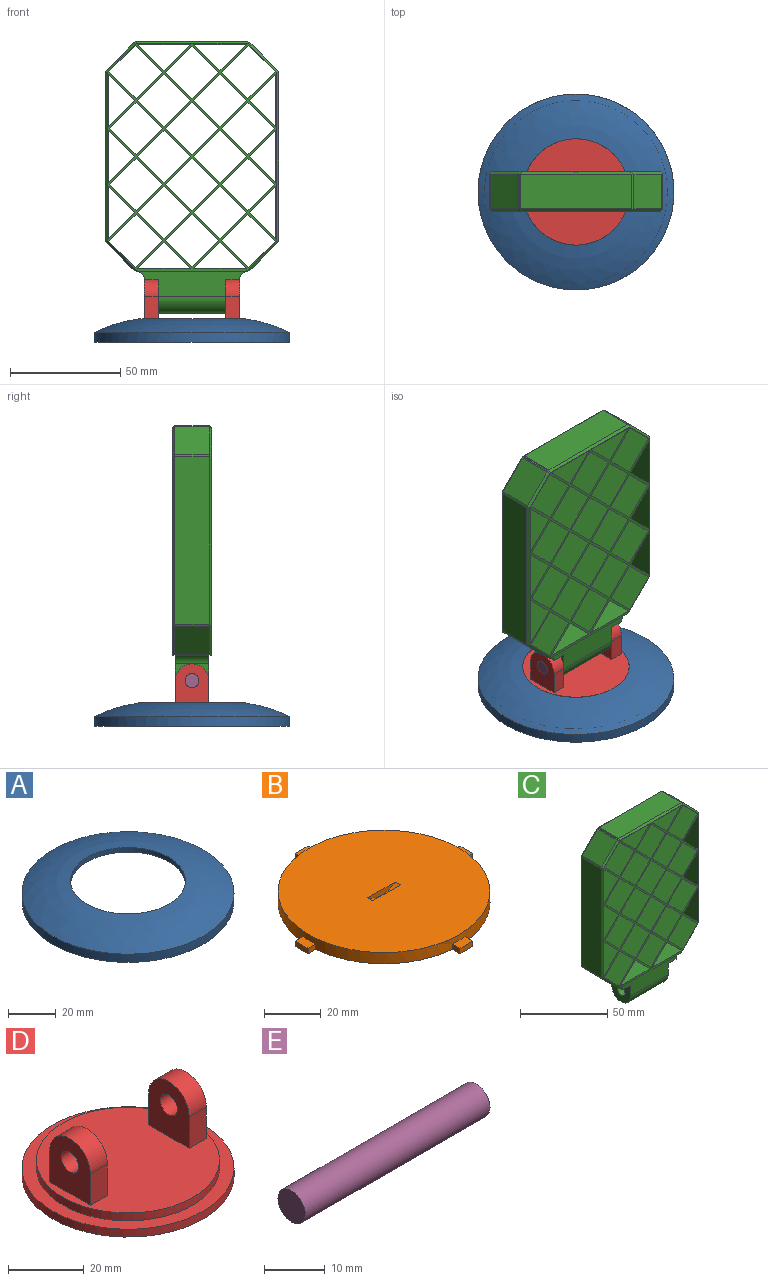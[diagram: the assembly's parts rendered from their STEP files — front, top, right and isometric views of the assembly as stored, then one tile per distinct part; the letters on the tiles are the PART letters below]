
ASSEMBLY  parts=5 mates=4
PART A: 24 faces, bbox 88.9x88.9x10.5 mm
  f0: cylinder r=38.1mm len=75.92mm, axis (0,0,-1), area 287.6mm2, adj f5,f6,f16,f21
  f1: cylinder r=38.1mm len=75.92mm, axis (0,0,-1), area 287.6mm2, adj f4,f7,f16,f22
  f2: plane 6.48x4.83mm, normal (1,0,0), area 20.8mm2, adj f3,f4,f5,f16,f17,f19,f20
  f3: plane 0.95x0.06mm, normal (0,0,-1), area 0mm2, adj f2,f5,f19
  f4: plane 4.83x3.38mm, normal (0,-1,0), area 8.7mm2, adj f1,f2,f16,f17,f19,f22
  f5: plane 4.83x3.38mm, normal (0,1,0), area 8.7mm2, adj f0,f2,f3,f16,f19,f21
  f6: plane 4.83x3.38mm, normal (0,1,0), area 8.7mm2, adj f0,f8,f9,f16,f19,f21
  f7: plane 4.83x3.38mm, normal (0,-1,0), area 8.7mm2, adj f1,f9,f16,f18,f19,f22
  f8: plane 0.95x0.06mm, normal (0,0,-1), area 0mm2, adj f6,f9,f19
  f9: plane 6.48x4.83mm, normal (-1,0,0), area 20.8mm2, adj f6,f7,f8,f16,f18,f19,f23
  f10: cylinder r=28.57mm len=57.15mm, axis (0,0,-1), area 547.2mm2, adj f13,f14
  f11: cylinder r=24.13mm len=48.26mm, axis (0,0,-1), area 360.4mm2, adj f13,f15
  f12: cylinder r=44.45mm len=88.9mm, axis (0,0,-1), area 1182.8mm2, adj f15,f16
  f13: plane 57.15x57.15mm, normal (0,0,-1), area 736mm2, adj f10,f11
  f14: plane 82.8x82.8mm, normal (0,0,-1), area 2819.9mm2, adj f10,f19
  f15: revolved ~88.9x88.9mm, area 9265.5mm2, adj f11,f12
  f16: plane 88.9x88.9mm, normal (0,0,-1), area 1604.3mm2, adj f0,f1,f2,f4,f5,f6,f7,f9
  f17: plane 0.95x0.06mm, normal (0,0,-1), area 0mm2, adj f2,f4,f19
  f18: plane 0.95x0.06mm, normal (0,0,-1), area 0mm2, adj f7,f9,f19
  f19: cylinder r=41.4mm len=82.8mm, axis (0,0,-1), area 652.1mm2, adj f2,f3,f4,f5,f6,f7,f8,f9
  f20: plane 4.58x0.06mm, normal (0,0,1), area 0.2mm2, adj f2,f19
  f21: plane 82.55x38.16mm, normal (0,0,1), area 390.9mm2, adj f0,f5,f6,f19
  f22: plane 82.55x38.16mm, normal (0,0,1), area 390.9mm2, adj f1,f4,f7,f19
  f23: plane 4.58x0.06mm, normal (0,0,1), area 0.2mm2, adj f9,f19
PART B: 28 faces, bbox 82.4x82.4x4.8 mm
  f0: plane 6.35x3.88mm, normal (0,0,1), area 23.8mm2, adj f12,f13,f14,f15
  f1: plane 6.35x3.88mm, normal (0,0,1), area 23.8mm2, adj f12,f16,f17,f18
  f2: plane 6.35x3.88mm, normal (0,0,1), area 23.8mm2, adj f9,f10,f11,f23
  f3: plane 6.35x2.29mm, normal (0,1,0), area 14.5mm2, adj f4,f19,f21,f24
  f4: plane 6.35x2.29mm, normal (1,0,0), area 14.5mm2, adj f3,f5,f21,f24
  f5: plane 6.35x2.29mm, normal (0,-1,0), area 14.5mm2, adj f4,f19,f21,f24
  f6: plane 3.76x2.29mm, normal (-1,0,0), area 8.6mm2, adj f7,f12,f20,f21
  f7: cylinder r=41.21mm len=6.35mm, axis (0,0,-1), area 14.5mm2, adj f6,f8,f20,f21
  f8: plane 3.76x2.29mm, normal (1,0,0), area 8.6mm2, adj f7,f12,f20,f21
  f9: plane 3.76x2.29mm, normal (0,-1,0), area 8.6mm2, adj f2,f10,f12,f21
  f10: cylinder r=41.21mm len=6.35mm, axis (0,0,-1), area 14.5mm2, adj f2,f9,f11,f21
  f11: plane 3.76x2.29mm, normal (0,1,0), area 8.6mm2, adj f2,f10,f12,f21
  f12: cylinder r=37.46mm len=74.93mm, axis (0,0,-1), area 1061.8mm2, adj f0,f1,f6,f8,f9,f11,f13,f15
  f13: plane 3.76x2.29mm, normal (1,0,0), area 8.6mm2, adj f0,f12,f14,f21
  f14: cylinder r=41.21mm len=6.35mm, axis (0,0,-1), area 14.5mm2, adj f0,f13,f15,f21
  f15: plane 3.76x2.29mm, normal (-1,0,0), area 8.6mm2, adj f0,f12,f14,f21
  f16: plane 3.76x2.29mm, normal (0,1,0), area 8.6mm2, adj f1,f12,f17,f21
  f17: cylinder r=41.21mm len=6.35mm, axis (0,0,-1), area 14.5mm2, adj f1,f16,f18,f21
  f18: plane 3.76x2.29mm, normal (0,-1,0), area 8.6mm2, adj f1,f12,f17,f21
  f19: plane 6.35x2.29mm, normal (-1,0,0), area 14.5mm2, adj f3,f5,f21,f24
  f20: plane 6.35x3.88mm, normal (0,0,1), area 23.8mm2, adj f6,f7,f8,f12
  f21: plane 82.42x82.42mm, normal (0,0,-1), area 4464.6mm2, adj f3,f4,f5,f6,f7,f8,f9,f10
  f22: plane 74.93x74.93mm, normal (0,0,1), area 4374.9mm2, adj f12,f23,f25,f26,f27
  f23: extruded ~6.35x2.54mm, area 16.1mm2, adj f2,f12,f22
  f24: plane 6.35x6.35mm, normal (0,0,-1), area 40.3mm2, adj f3,f4,f5,f19
  f25: cylinder r=11.43mm len=13.65mm, axis (0,1,0), area 37.2mm2, adj f22,f26,f27
  f26: plane 13.65x2.26mm, normal (0,1,0), area 21mm2, adj f22,f25
  f27: plane 13.65x2.26mm, normal (0,-1,0), area 21mm2, adj f22,f25
PART C: 153 faces, bbox 78.7x17.8x123.2 mm
  f0: plane 15.24x15.11mm, normal (1,0,0), area 174.2mm2, adj f1,f2,f3,f129,f130
  f1: plane 50.8x11.49mm, normal (0,1,0), area 404.9mm2, adj f0,f3,f4,f125,f126,f127,f128,f129
  f2: plane 50.8x11.49mm, normal (0,-1,0), area 404.9mm2, adj f0,f3,f5,f125,f126,f127,f128,f129
  f3: plane 15.11x6.35mm, normal (0,0,-1), area 96mm2, adj f0,f1,f2,f127
  f4: plane 50.8x1.33mm, normal (0,0,-1), area 67.2mm2, adj f1,f17,f18,f124,f136,f152
  f5: plane 50.8x1.33mm, normal (0,0,-1), area 67.2mm2, adj f2,f17,f18,f123,f131,f132
  f6: plane 76.2x15.75mm, normal (1,0,0), area 1200mm2, adj f7,f122,f134,f151
  f7: plane 16.12x0.9mm, normal (0.92,0,0.38), area 15.5mm2, adj f6,f8,f134,f137,f150,f151
  f8: plane 15.75x12.7mm, normal (0.71,0,0.71), area 282.8mm2, adj f7,f9,f137,f150
  f9: plane 16.12x0.9mm, normal (0.38,0,0.92), area 15.5mm2, adj f8,f10,f137,f140,f149,f150
  f10: plane 50.6x15.75mm, normal (0,0,1), area 796.8mm2, adj f9,f140,f146,f149
  f11: plane 15.75x0.52mm, normal (-0.38,0,0.92), area 8.9mm2, adj f141,f142,f146,f147
  f12: plane 15.75x12.56mm, normal (-0.71,0,0.71), area 279.7mm2, adj f13,f135,f142,f143
  f13: plane 16.12x0.9mm, normal (-0.92,0,0.38), area 15.5mm2, adj f12,f14,f133,f135,f139,f143
  f14: plane 76.2x15.75mm, normal (-1,0,0), area 1200mm2, adj f13,f15,f133,f139
  f15: plane 16.12x0.9mm, normal (-0.92,0,-0.38), area 15.5mm2, adj f14,f16,f131,f133,f136,f139
  f16: plane 15.75x12.7mm, normal (-0.71,0,-0.71), area 282.8mm2, adj f15,f17,f131,f136
  f17: plane 16.49x0.9mm, normal (-0.38,0,-0.92), area 15.7mm2, adj f4,f5,f16,f126,f131,f136
  f18: plane 16.49x0.9mm, normal (0.38,0,-0.92), area 15.7mm2, adj f4,f5,f19,f127,f132,f152
  f19: plane 15.75x12.7mm, normal (0.71,0,-0.71), area 282.8mm2, adj f18,f122,f132,f152
  f20: plane 17.78x11.98mm, normal (0.71,0,-0.71), area 301.3mm2, adj f21,f94,f123,f124
  f21: plane 17.78x12.34mm, normal (-0.71,0,-0.71), area 310.3mm2, adj f20,f22,f123,f124
  f22: plane 17.78x11.98mm, normal (-0.71,0,0.71), area 301.3mm2, adj f21,f94,f123,f124
  f23: plane 17.78x11.98mm, normal (-0.71,0,0.71), area 301.3mm2, adj f24,f95,f123,f124
  f24: plane 17.78x11.98mm, normal (0.71,0,0.71), area 301.3mm2, adj f23,f25,f123,f124
  f25: plane 17.78x11.98mm, normal (0.71,0,-0.71), area 301.3mm2, adj f24,f95,f123,f124
  f26: plane 23.96x17.78mm, normal (1,0,0), area 426.1mm2, adj f27,f96,f123,f124
  f27: plane 17.78x11.98mm, normal (-0.71,0,-0.71), area 301.3mm2, adj f26,f96,f123,f124
  f28: plane 17.78x11.98mm, normal (-0.71,0,-0.71), area 301.3mm2, adj f29,f97,f123,f124
  f29: plane 17.78x11.98mm, normal (-0.71,0,0.71), area 301.3mm2, adj f28,f30,f123,f124
  f30: plane 17.78x11.98mm, normal (0.71,0,0.71), area 301.3mm2, adj f29,f97,f123,f124
  f31: plane 17.78x11.98mm, normal (0.71,0,-0.71), area 301.3mm2, adj f32,f98,f123,f124
  f32: plane 17.78x11.98mm, normal (-0.71,0,-0.71), area 301.2mm2, adj f31,f33,f123,f124
  f33: plane 17.78x11.98mm, normal (-0.71,0,0.71), area 301.3mm2, adj f32,f98,f123,f124
  f34: plane 17.78x11.98mm, normal (-0.71,0,-0.71), area 301.2mm2, adj f35,f99,f123,f124
  f35: plane 17.78x11.98mm, normal (-0.71,0,0.71), area 301.3mm2, adj f34,f36,f123,f124
  f36: plane 17.78x11.98mm, normal (0.71,0,0.71), area 301.2mm2, adj f35,f99,f123,f124
  f37: plane 23.96x17.78mm, normal (0,0,1), area 426.1mm2, adj f38,f100,f123,f124
  f38: plane 17.78x11.98mm, normal (0.71,0,-0.71), area 301.3mm2, adj f37,f100,f123,f124
  f39: plane 17.78x11.98mm, normal (-0.71,0,-0.71), area 301.3mm2, adj f40,f101,f123,f124
  f40: plane 17.78x11.98mm, normal (-0.71,0,0.71), area 301.3mm2, adj f39,f41,f123,f124
  f41: plane 17.78x11.98mm, normal (0.71,0,0.71), area 301.3mm2, adj f40,f101,f123,f124
  f42: plane 17.78x11.98mm, normal (0.71,0,-0.71), area 301.3mm2, adj f43,f102,f123,f124
  f43: plane 23.96x17.78mm, normal (-1,0,0), area 426.1mm2, adj f42,f102,f123,f124
  f44: plane 23.96x17.78mm, normal (0,0,1), area 425.9mm2, adj f45,f103,f123,f124
  f45: plane 17.78x11.98mm, normal (0.71,0,-0.71), area 301.2mm2, adj f44,f103,f123,f124
  f46: plane 23.96x17.78mm, normal (1,0,0), area 425.9mm2, adj f47,f104,f123,f124
  f47: plane 17.78x11.98mm, normal (-0.71,0,-0.71), area 301.2mm2, adj f46,f104,f123,f124
  f48: plane 17.78x11.98mm, normal (0.71,0,-0.71), area 301.3mm2, adj f49,f105,f123,f124
  f49: plane 17.78x11.98mm, normal (-0.71,0,-0.71), area 301.3mm2, adj f48,f50,f123,f124
  f50: plane 17.78x11.98mm, normal (-0.71,0,0.71), area 301.3mm2, adj f49,f105,f123,f124
  f51: plane 17.78x11.98mm, normal (0.71,0,0.71), area 301.3mm2, adj f52,f106,f123,f124
  f52: plane 17.78x12.34mm, normal (0.71,0,-0.71), area 310.2mm2, adj f51,f53,f123,f124
  f53: plane 17.78x11.98mm, normal (-0.71,0,-0.71), area 301.3mm2, adj f52,f106,f123,f124
  f54: plane 17.78x11.98mm, normal (0.71,0,-0.71), area 301.3mm2, adj f55,f107,f123,f124
  f55: plane 17.78x11.98mm, normal (-0.71,0,-0.71), area 301.3mm2, adj f54,f56,f123,f124
  f56: plane 17.78x11.98mm, normal (-0.71,0,0.71), area 301.3mm2, adj f55,f107,f123,f124
  f57: plane 17.78x11.98mm, normal (-0.71,0,0.71), area 301.3mm2, adj f58,f108,f123,f124
  f58: plane 17.78x11.98mm, normal (0.71,0,0.71), area 301.3mm2, adj f57,f59,f123,f124
  f59: plane 17.78x11.98mm, normal (0.71,0,-0.71), area 301.3mm2, adj f58,f108,f123,f124
  f60: plane 17.78x12.34mm, normal (-0.71,0,-0.71), area 310.3mm2, adj f61,f109,f123,f124
  f61: plane 17.78x11.98mm, normal (-0.71,0,0.71), area 301.3mm2, adj f60,f62,f123,f124
  f62: plane 17.78x12.34mm, normal (0.71,0,0.71), area 310.3mm2, adj f61,f109,f123,f124
  f63: plane 17.78x11.98mm, normal (-0.71,0,0.71), area 301.3mm2, adj f64,f110,f123,f124
  f64: plane 17.78x11.98mm, normal (0.71,0,0.71), area 301.3mm2, adj f63,f65,f123,f124
  f65: plane 17.78x11.98mm, normal (0.71,0,-0.71), area 301.3mm2, adj f64,f110,f123,f124
  f66: plane 17.78x11.98mm, normal (0.71,0,0.71), area 301.3mm2, adj f67,f111,f123,f124
  f67: plane 17.78x11.98mm, normal (0.71,0,-0.71), area 301.3mm2, adj f66,f68,f123,f124
  f68: plane 17.78x11.98mm, normal (-0.71,0,-0.71), area 301.2mm2, adj f67,f111,f123,f124
  f69: plane 23.96x17.78mm, normal (1,0,0), area 426.1mm2, adj f70,f112,f123,f124
  f70: plane 17.78x11.98mm, normal (-0.71,0,-0.71), area 301.3mm2, adj f69,f112,f123,f124
  f71: plane 17.78x11.98mm, normal (-0.71,0,-0.71), area 301.2mm2, adj f72,f113,f123,f124
  f72: plane 17.78x11.98mm, normal (-0.71,0,0.71), area 301.3mm2, adj f71,f73,f123,f124
  f73: plane 17.78x11.98mm, normal (0.71,0,0.71), area 301.2mm2, adj f72,f113,f123,f124
  f74: plane 17.78x11.98mm, normal (0.71,0,0.71), area 301.2mm2, adj f75,f114,f123,f124
  f75: plane 17.78x11.98mm, normal (0.71,0,-0.71), area 301.3mm2, adj f74,f76,f123,f124
  f76: plane 17.78x11.98mm, normal (-0.71,0,-0.71), area 301.2mm2, adj f75,f114,f123,f124
  f77: plane 17.78x11.98mm, normal (0.71,0,-0.71), area 301.3mm2, adj f78,f115,f123,f124
  f78: plane 17.78x11.98mm, normal (-0.71,0,-0.71), area 301.3mm2, adj f77,f79,f123,f124
  f79: plane 17.78x11.98mm, normal (-0.71,0,0.71), area 301.3mm2, adj f78,f115,f123,f124
  f80: plane 17.78x11.98mm, normal (0.71,0,0.71), area 301.2mm2, adj f81,f116,f123,f124
  f81: plane 17.78x11.98mm, normal (0.71,0,-0.71), area 301.3mm2, adj f80,f82,f123,f124
  f82: plane 17.78x11.98mm, normal (-0.71,0,-0.71), area 301.2mm2, adj f81,f116,f123,f124
  f83: plane 17.78x11.98mm, normal (0.71,0,-0.71), area 301.3mm2, adj f84,f117,f123,f124
  f84: plane 23.96x17.78mm, normal (-1,0,0), area 426.1mm2, adj f83,f117,f123,f124
  f85: plane 17.78x11.98mm, normal (0.71,0,-0.71), area 301.3mm2, adj f86,f118,f123,f124
  f86: plane 23.96x17.78mm, normal (-1,0,0), area 426.1mm2, adj f85,f118,f123,f124
  f87: plane 17.78x12.34mm, normal (0.71,0,-0.71), area 310.3mm2, adj f88,f119,f123,f124
  f88: plane 17.78x11.98mm, normal (-0.71,0,-0.71), area 301.3mm2, adj f87,f89,f123,f124
  f89: plane 17.78x12.34mm, normal (-0.71,0,0.71), area 310.3mm2, adj f88,f119,f123,f124
  f90: plane 17.78x11.98mm, normal (0.71,0,0.71), area 301.2mm2, adj f91,f120,f123,f124
  f91: plane 23.96x17.78mm, normal (0,0,-1), area 425.9mm2, adj f90,f120,f123,f124
  f92: plane 17.78x11.98mm, normal (0.71,0,0.71), area 301.3mm2, adj f93,f121,f123,f124
  f93: plane 23.96x17.78mm, normal (0,0,-1), area 426.1mm2, adj f92,f121,f123,f124
  f94: plane 17.78x12.34mm, normal (0.71,0,0.71), area 310.3mm2, adj f20,f22,f123,f124
  f95: plane 17.78x11.98mm, normal (-0.71,0,-0.71), area 301.3mm2, adj f23,f25,f123,f124
  f96: plane 17.78x11.98mm, normal (-0.71,0,0.71), area 301.3mm2, adj f26,f27,f123,f124
  f97: plane 17.78x11.98mm, normal (0.71,0,-0.71), area 301.3mm2, adj f28,f30,f123,f124
  f98: plane 17.78x11.98mm, normal (0.71,0,0.71), area 301.2mm2, adj f31,f33,f123,f124
  f99: plane 17.78x11.98mm, normal (0.71,0,-0.71), area 301.3mm2, adj f34,f36,f123,f124
  f100: plane 17.78x11.98mm, normal (-0.71,0,-0.71), area 301.3mm2, adj f37,f38,f123,f124
  f101: plane 17.78x11.98mm, normal (0.71,0,-0.71), area 301.3mm2, adj f39,f41,f123,f124
  f102: plane 17.78x11.98mm, normal (0.71,0,0.71), area 301.3mm2, adj f42,f43,f123,f124
  f103: plane 17.78x11.98mm, normal (-0.71,0,-0.71), area 301.2mm2, adj f44,f45,f123,f124
  f104: plane 17.78x11.98mm, normal (-0.71,0,0.71), area 301.2mm2, adj f46,f47,f123,f124
  f105: plane 17.78x11.98mm, normal (0.71,0,0.71), area 301.3mm2, adj f48,f50,f123,f124
  f106: plane 17.78x12.34mm, normal (-0.71,0,0.71), area 310.2mm2, adj f51,f53,f123,f124
  f107: plane 17.78x11.98mm, normal (0.71,0,0.71), area 301.3mm2, adj f54,f56,f123,f124
  f108: plane 17.78x11.98mm, normal (-0.71,0,-0.71), area 301.3mm2, adj f57,f59,f123,f124
  f109: plane 17.78x11.98mm, normal (0.71,0,-0.71), area 301.3mm2, adj f60,f62,f123,f124
  f110: plane 17.78x11.98mm, normal (-0.71,0,-0.71), area 301.3mm2, adj f63,f65,f123,f124
  f111: plane 17.78x11.98mm, normal (-0.71,0,0.71), area 301.3mm2, adj f66,f68,f123,f124
  f112: plane 17.78x11.98mm, normal (-0.71,0,0.71), area 301.3mm2, adj f69,f70,f123,f124
  f113: plane 17.78x11.98mm, normal (0.71,0,-0.71), area 301.3mm2, adj f71,f73,f123,f124
  f114: plane 17.78x11.98mm, normal (-0.71,0,0.71), area 301.3mm2, adj f74,f76,f123,f124
  f115: plane 17.78x11.98mm, normal (0.71,0,0.71), area 301.2mm2, adj f77,f79,f123,f124
  f116: plane 17.78x11.98mm, normal (-0.71,0,0.71), area 301.3mm2, adj f80,f82,f123,f124
  f117: plane 17.78x11.98mm, normal (0.71,0,0.71), area 301.3mm2, adj f83,f84,f123,f124
  f118: plane 17.78x11.98mm, normal (0.71,0,0.71), area 301.3mm2, adj f85,f86,f123,f124
  f119: plane 17.78x11.98mm, normal (0.71,0,0.71), area 301.3mm2, adj f87,f89,f123,f124
  f120: plane 17.78x11.98mm, normal (-0.71,0,0.71), area 301.2mm2, adj f90,f91,f123,f124
  f121: plane 17.78x11.98mm, normal (-0.71,0,0.71), area 301.3mm2, adj f92,f93,f123,f124
  f122: plane 16.12x0.9mm, normal (0.92,0,-0.38), area 15.5mm2, adj f6,f19,f132,f134,f151,f152
  f123: plane 103.12x76.71mm, normal (0,-1,0), area 915.6mm2, adj f5,f20,f21,f22,f23,f24,f25,f26
  f124: plane 103.12x76.71mm, normal (0,1,0), area 915.6mm2, adj f4,f20,f21,f22,f23,f24,f25,f26
  f125: plane 15.11x6.35mm, normal (0,0,-1), area 96mm2, adj f1,f2,f126,f128
  f126: cylinder r=3.81mm len=15.11mm, axis (0,1,0), area 90.4mm2, adj f1,f2,f17,f125
  f127: cylinder r=3.81mm len=15.11mm, axis (0,-1,0), area 90.4mm2, adj f1,f2,f3,f18
  f128: plane 15.24x15.11mm, normal (-1,0,0), area 174.2mm2, adj f1,f2,f125,f129,f130
  f129: cylinder r=7.56mm len=30.48mm, axis (-1,0,0), area 723.6mm2, adj f0,f1,f2,f128
  f130: cylinder r=3.17mm len=30.48mm, axis (-1,0,0), area 607.1mm2, adj f0,f128
  f131: plane 14.7x13.86mm, normal (-0.5,-0.71,-0.5), area 27.5mm2, adj f5,f15,f16,f17,f123,f133
  f132: plane 14.7x13.86mm, normal (0.5,-0.71,-0.5), area 27.5mm2, adj f5,f18,f19,f122,f123,f134
  f133: plane 77.1x1.02mm, normal (-0.71,-0.71,0), area 110.3mm2, adj f13,f14,f15,f123,f131,f135
  f134: plane 77.1x1.02mm, normal (0.71,-0.71,0), area 110.3mm2, adj f6,f7,f122,f123,f132,f137
  f135: plane 13.46x13.35mm, normal (-0.5,-0.71,0.5), area 25.9mm2, adj f12,f13,f123,f133,f138
  f136: plane 14.7x13.86mm, normal (-0.5,0.71,-0.5), area 27.5mm2, adj f4,f15,f16,f17,f124,f139
  f137: plane 13.68x13.68mm, normal (0.5,-0.71,0.5), area 26.6mm2, adj f7,f8,f9,f123,f134,f140
  f138: plane 1.02x0.94mm, normal (-0.4,-0.7,0.59), area 0.3mm2, adj f135,f141,f142
  f139: plane 77.1x1.02mm, normal (-0.71,0.71,0), area 110.3mm2, adj f13,f14,f15,f124,f136,f143
  f140: plane 51.05x1.02mm, normal (0,-0.71,0.71), area 73.1mm2, adj f9,f10,f123,f137,f144
  f141: plane 1.16x1.02mm, normal (-0.27,-0.71,0.65), area 0.8mm2, adj f11,f123,f138,f144
  f142: plane 15.75x0.33mm, normal (-0.56,0,0.83), area 6.2mm2, adj f11,f12,f138,f145
  f143: plane 13.46x13.35mm, normal (-0.5,0.71,0.5), area 25.9mm2, adj f12,f13,f124,f139,f145
  f144: plane 1.02x1.02mm, normal (-0.14,-0.7,0.7), area 0.3mm2, adj f140,f141,f146
  f145: plane 1.02x0.94mm, normal (-0.4,0.7,0.59), area 0.3mm2, adj f142,f143,f147
  f146: plane 15.75x0.39mm, normal (-0.2,0,0.98), area 6.2mm2, adj f10,f11,f144,f148
  f147: plane 1.16x1.02mm, normal (-0.27,0.71,0.65), area 0.8mm2, adj f11,f124,f145,f148
  f148: plane 1.02x1.02mm, normal (-0.14,0.7,0.7), area 0.3mm2, adj f146,f147,f149
  f149: plane 51.05x1.02mm, normal (0,0.71,0.71), area 73.1mm2, adj f9,f10,f124,f148,f150
  f150: plane 13.68x13.68mm, normal (0.5,0.71,0.5), area 26.6mm2, adj f7,f8,f9,f124,f149,f151
  f151: plane 77.1x1.02mm, normal (0.71,0.71,0), area 110.3mm2, adj f6,f7,f122,f124,f150,f152
  f152: plane 14.7x13.86mm, normal (0.5,0.71,-0.5), area 27.5mm2, adj f4,f18,f19,f122,f124,f151
PART D: 17 faces, bbox 55.9x55.9x22.8 mm
  f0: plane 55.88x55.88mm, normal (0,0,1), area 623.3mm2, adj f1,f4
  f1: cylinder r=27.94mm len=55.88mm, axis (0,0,-1), area 445.9mm2, adj f0,f2
  f2: plane 55.88x55.88mm, normal (0,0,-1), area 2452.5mm2, adj f1
  f3: plane 48.26x48.26mm, normal (0,0,1), area 1637.3mm2, adj f4,f7,f8,f9,f10,f13,f14,f15
  f4: cylinder r=24.13mm len=48.26mm, axis (0,0,-1), area 385.1mm2, adj f0,f3
  f5: cylinder r=3.17mm len=6.35mm, axis (1,0,0), area 126.7mm2, adj f7,f8
  f6: cylinder r=7.56mm len=15.11mm, axis (1,0,0), area 150.7mm2, adj f7,f8,f9,f10
  f7: plane 17.72x15.11mm, normal (-1,0,0), area 211.6mm2, adj f3,f5,f6,f9,f10
  f8: plane 17.72x15.11mm, normal (1,0,0), area 211.6mm2, adj f3,f5,f6,f9,f10
  f9: plane 10.16x6.35mm, normal (0,-1,0), area 64.5mm2, adj f3,f6,f7,f8
  f10: plane 10.16x6.35mm, normal (0,1,0), area 64.5mm2, adj f3,f6,f7,f8
  f11: cylinder r=7.56mm len=15.11mm, axis (1,0,0), area 150.7mm2, adj f13,f14,f15,f16
  f12: cylinder r=3.17mm len=6.35mm, axis (1,0,0), area 126.7mm2, adj f13,f14
  f13: plane 17.72x15.11mm, normal (-1,0,0), area 211.6mm2, adj f3,f11,f12,f15,f16
  f14: plane 17.72x15.11mm, normal (1,0,0), area 211.6mm2, adj f3,f11,f12,f15,f16
  f15: plane 10.16x6.35mm, normal (0,-1,0), area 64.5mm2, adj f3,f11,f13,f14
  f16: plane 10.16x6.35mm, normal (0,1,0), area 64.5mm2, adj f3,f11,f13,f14
PART E: 3 faces, bbox 43.2x6.4x6.4 mm
  f0: cylinder r=3.17mm len=43.18mm, axis (-1,0,0), area 861.4mm2, adj f1,f2
  f1: plane 6.35x6.35mm, normal (1,0,0), area 31.7mm2, adj f0
  f2: plane 6.35x6.35mm, normal (-1,0,0), area 31.7mm2, adj f0
PLACE A rot(axis=(0,-1,0),0deg) t=(74.06,42.92,-15.48)mm
PLACE B rot(axis=(0,-1,0),0deg) t=(74.06,42.92,-17.9)mm
PLACE C t=(86.76,51.81,-5.78)mm
PLACE D t=(74.06,42.92,-12.52)mm
PLACE E t=(52.47,42.92,2.72)mm
MATE revolute D.f4 <-> A.f11  axis (0,0,-1) through (74.06,42.92,-8.71)mm
MATE fastened E.f0 <-> D.f5  axis (-1,0,0) through (52.47,42.92,2.72)mm
MATE revolute C.f129 <-> E.f0  axis (-1,0,0) through (74.06,42.92,2.72)mm
MATE revolute B.f7 <-> A.f0  axis (0,0,-1) through (74.06,42.92,-16.75)mm
